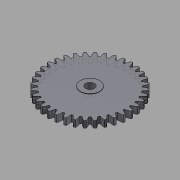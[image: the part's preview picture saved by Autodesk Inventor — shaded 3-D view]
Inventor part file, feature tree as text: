
AUTODESK INVENTOR PART (.ipt)
format: ipt  version: 2015 (Build 190159000, 159)  size: 313,856 bytes
history: native  units: in
note: dims shown in document units (in); Inventor stores cm internally (conversion verified against a paired STEP export)
features: other x13, sketch x4, plane x2
ambient origin geometry x8: Origin, YZ Plane, XZ Plane, XY Plane, X Axis, Y Axis, Z Axis, Center Point
bodies: Solid1 (feature_tree)
feature tree (19):
  other  "Spur Gear2"
  other  "Solid1::Spur Gear2"
  other  "TaggingFeature1"
  sketch  "Sketch1"  dims[d0=0.3937in]
  sketch  "Sketch2"  dims[d16=0.4528in d17=0.0in d41=0.0in d43=0.4528in d46=0.4528in d47=0.0in d48=0.0in]
  sketch  "Sketch3"
  sketch  "Sketch4"
  plane  "XZ Plane_1"
  plane  "Work Plane2"
  other  "Z Axis_1"
  other  "Srf1"
  other  "Srf1::Derived"
  other  "Distance iMate"
  other  "Align iMate"
  other  "Mesh iMate"
  other  "Axis iMate"
  other  "Position iMate"
  other  "Mesh iMate2"
  other  "Start plane iMate"
